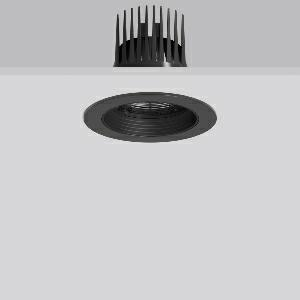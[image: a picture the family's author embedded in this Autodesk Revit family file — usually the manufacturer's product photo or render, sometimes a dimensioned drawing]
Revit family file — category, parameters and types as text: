
# Revit family: heledon_maxi_e_901768_003_3_76_e68a
name_source: partatom
category: Lighting Fixtures
units: mm (PartAtom-declared; Revit-internal decimal feet)

## family parameters
Cut with Voids When Loaded = No
Host = Face
Light Source = No
Part Type = Normal
Room Calculation Point = No
Round Connector Dimension = Use Diameter
Shared = No

## types (1)
- HELEDON maxi E (1 x LED Modul 935, 3600 lm, 3500)
    Apparent Load = 35 VA
    Approval mark = CE
    CIE Flux Codes = 96 100 100 100 100
    Color Rendering = 92
    Color Temperature = 3500
    Default Elevation = 1800 mm
    Description = Series: HELEDON maxi
Round recessed downlight. Housing: die-cast aluminium, powder-coated. Black plastic ring and recessed LED to prevent glare from the side. Optical assembly with lens made of plastic (polycarbonate) for the best homogeneous light distribution - can be changed without tools. Best colour rendering index Ra>90. Suitable for Recessed ceiling mounting. Installation without tools thanks to spring fastening system. Including separate LED converter with connecting cable 600 mm.High quality converter without flickering and stroboscopic effect. Through-wiring box (5 pole) available as accessory. The following accessories can be mounted without use of tools: interchangeable lenses, decorative glasses, honeycomb louvre, clear and frosted diffusers, white interchangeable plastic ring. 
Colour: deep black, matt (RAL 9005)
Diameter: 162 mm
Height: 3 mm
Cut-out diameter: 152 mm
Recess height: 200 mm
Luminaire: recess height: 135 mm
Lamp: LED
Socket: without socket
Colour temperature: 3500K
Colour rendering index (CRI): 92
System power: 35 W
Rated luminous flux: 3600 lm
Luminous efficiency: 103 lm/W
Control gear: Converter, dimmable, DALI
Protection class: II
Type of protection: IP 20
    Height = 0 mm  [stored 0 ft]
    Lamp = 1 x LED Modul 935
    Lamp Light Flux = 3600 lm
    Lamp count = 1
    Length = 162 mm
    Lifetime = 50000 h
    Luminous efficacy = 103 lm/W
    Manufacturer = RZB
    ModVariant = No
    Model = 901768.003.3.76
    Mounting Place = Ceiling
    Mounting Type = Recessed
    Number of Poles = 1
    OnlyDefault = Yes
    Power Factor = 1
    Product Name = HELEDON maxi E
    Product group = Recessed downlights
    ProductGroupID = 402
    Protection Class = Protection class II
    Protection Degree = IP 20
    RLX_Detail_Level = 1
    RLX_Emergency_Light_Flux = 0 lm
    RLX_Emergency_Type = 0
    RLX_Emergency_Type_DB = No
    RlxData = <blob elided: 123813 chars, md5=36a59cb4>
    Socket = socket
    Standby Power = 0 W
    System Light Flux = 3600 lm
    System Power = 35 W
    Type Comments = Product without accessories
    Type Image = 901663.003.jpg
    URL = http://relux.com
    VarID = ---
    Voltage = 230 V
    Voltage Range = 220-240 V
    Weight = 0.00 kg
    Width = 0 mm  [stored 0 ft]

note: [stored X ft] marks values corroborated as IEEE doubles in the binary element streams (Revit-internal decimal feet)

## geometry (parser evidence)
native form markers: Blend x4, Sweep x11
no freeform markers — native parametric forms only
